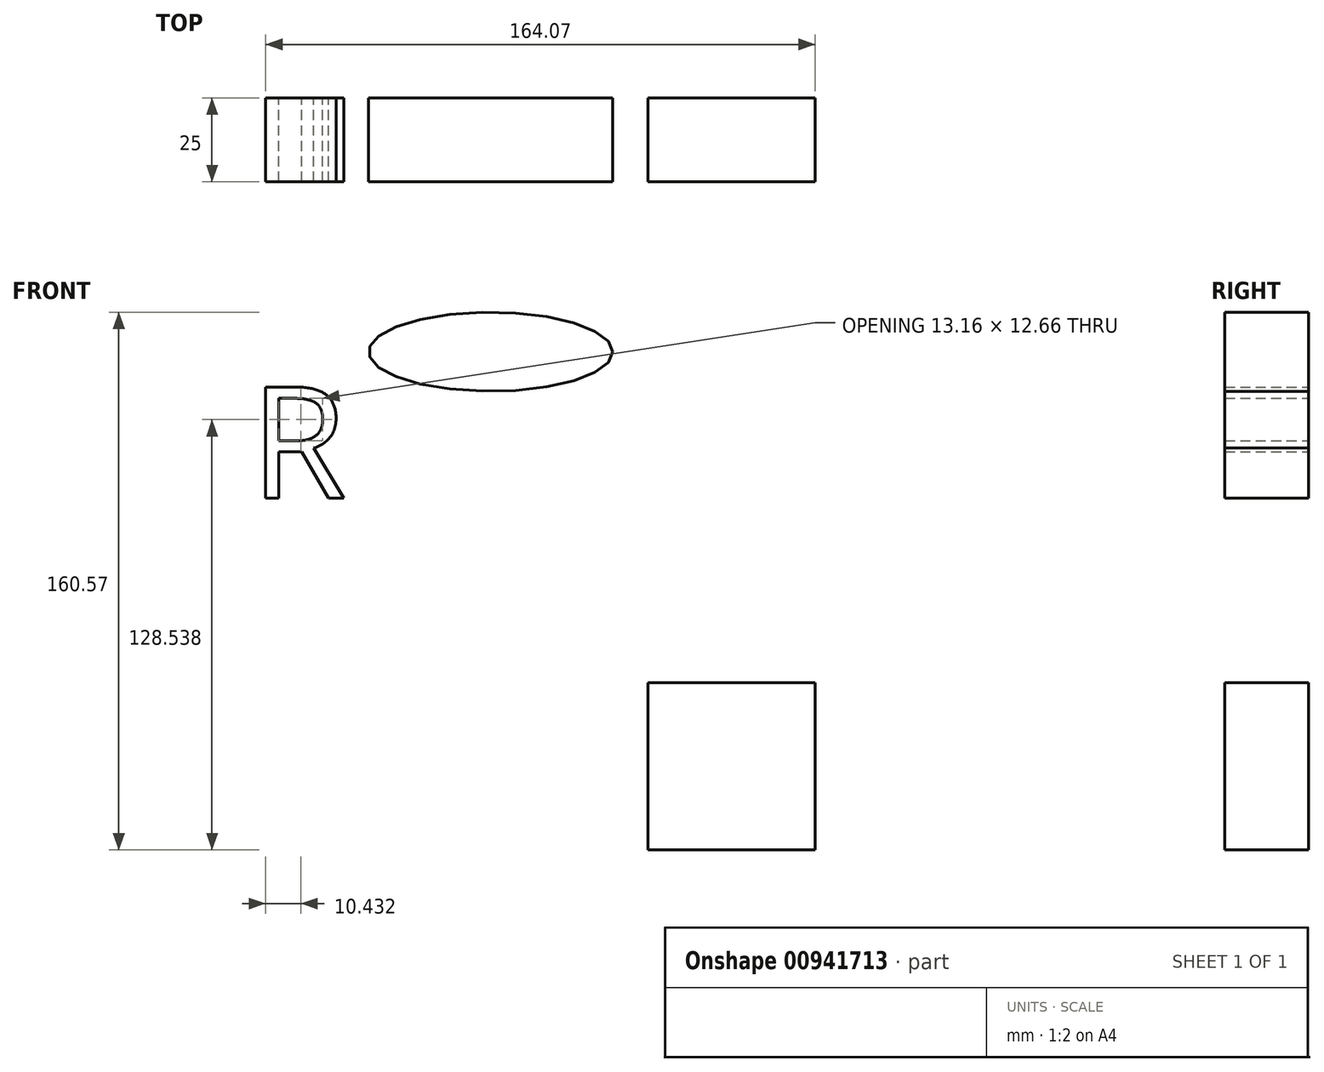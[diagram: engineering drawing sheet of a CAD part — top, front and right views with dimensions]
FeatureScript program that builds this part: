
annotation { "Feature Type Name" : "Feature", "Feature Type Description" : "" }
export const myFeature = defineFeature(function(context is Context, id is Id, definition is map)
    precondition{}
    {
        {
            var Q0;
            Q0=qCreatedBy(makeId("Front.planeOp"),FACE);
            var sketch = newSketch(context, id + "F0", { "sketchPlane" : qUnion([Q0])});
            skLineSegment(sketch, "E0.bottom", {"start": v(-20.96, -14.76) * mm, "end": v(29.04, -14.76) * mm});
            skLineSegment(sketch, "E0.top", {"start": v(-20.96, -64.76) * mm, "end": v(29.04, -64.76) * mm});
            skLineSegment(sketch, "E0.left", {"start": v(-20.96, -14.76) * mm, "end": v(-20.96, -64.76) * mm});
            skLineSegment(sketch, "E0.right", {"start": v(29.04, -14.76) * mm, "end": v(29.04, -64.76) * mm});
            skSolve(sketch);
        }
        {
            var Q0;
            Q0 = qSketchRegion(id + "F0", true);
            extrude(context, id + "F1", {"entities" : qUnion([Q0]), "depth" : 25 * mm, "offsetDistance" : 25 * mm});
        }
        {
            var Q0;
            Q0=qCreatedBy(makeId("Front.planeOp"),FACE);
            var sketch = newSketch(context, id + "F2", { "sketchPlane" : qUnion([Q0])});
            skText(sketch, "E1", { "text": "R\n", "fontName": "OpenSans-Regular.ttf"});
            const initialGuessF2  = {"E1": [-0.13958, 0.04037, 1, 0, 0.0334]};
            skSetInitialGuess(sketch, initialGuessF2);
            skSolve(sketch);
        }
        {
            var Q0;
            Q0 = qSketchRegion(id + "F2", true);
            extrude(context, id + "F3", {"entities" : qUnion([Q0]), "depth" : 25 * mm, "offsetDistance" : 25 * mm});
        }
        {
            var Q0;
            Q0=qCreatedBy(makeId("Front.planeOp"),FACE);
            var sketch = newSketch(context, id + "F4", { "sketchPlane" : qUnion([Q0])});
            skEllipse(sketch, "E2", {"center": v(-67.85, 84.03) * mm, "majorRadius": 36.44 * mm, "minorRadius": 11.78 * mm, "majorAxis": v(1, 0)});
            skSolve(sketch);
        }
        {
            var Q0;
            Q0 = qSketchRegion(id + "F4", true);
            extrude(context, id + "F5", {"entities" : qUnion([Q0]), "depth" : 25 * mm, "offsetDistance" : 25 * mm});
        }
    });
